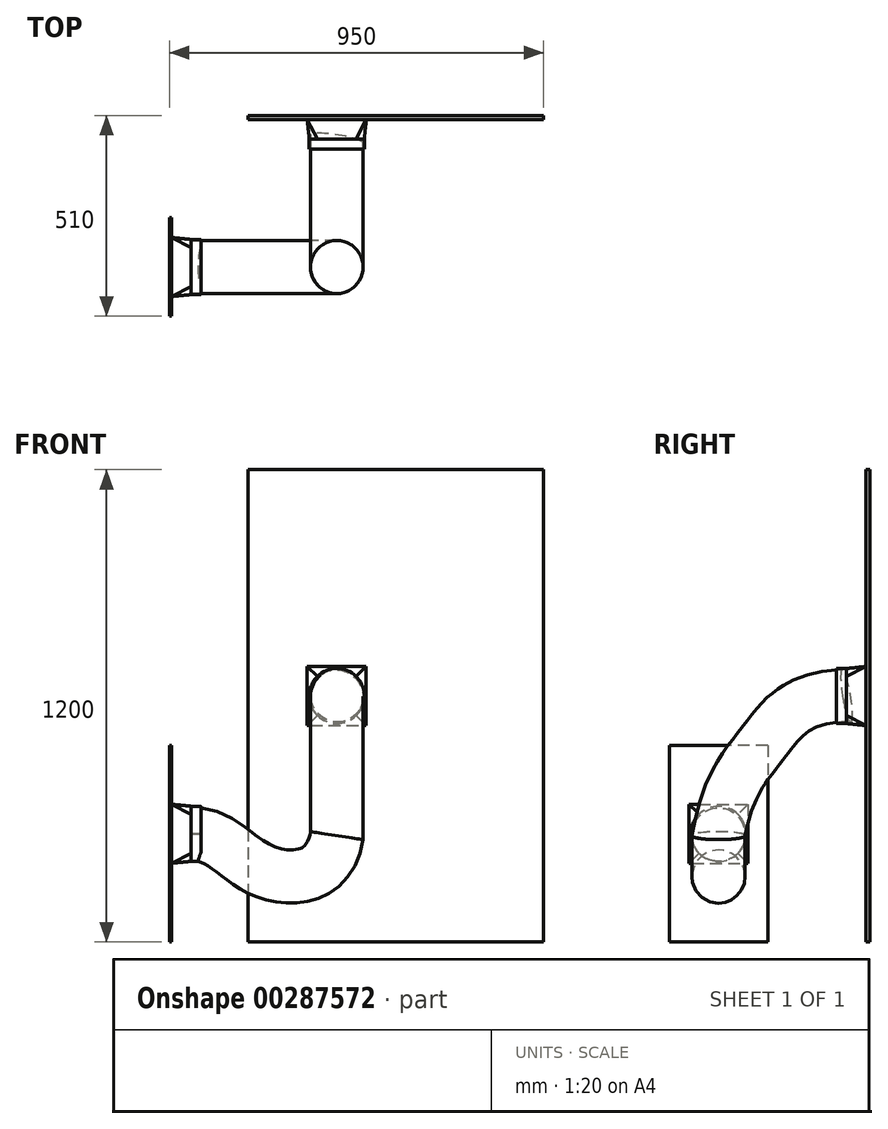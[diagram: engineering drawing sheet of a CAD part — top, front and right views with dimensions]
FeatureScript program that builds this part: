
annotation { "Feature Type Name" : "Feature", "Feature Type Description" : "" }
export const myFeature = defineFeature(function(context is Context, id is Id, definition is map)
    precondition{}
    {
        {
            var Q0;
            Q0=qCreatedBy(makeId("Top.planeOp"),FACE);
            var sketch = newSketch(context, id + "F0", { "sketchPlane" : qUnion([Q0])});
            skLineSegment(sketch, "E0.bottom", {"start": v(450, 450) * mm, "end": v(455, 450) * mm});
            skLineSegment(sketch, "E0.top", {"start": v(450, 200) * mm, "end": v(455, 200) * mm});
            skLineSegment(sketch, "E0.left", {"start": v(450, 450) * mm, "end": v(450, 200) * mm});
            skLineSegment(sketch, "E0.right", {"start": v(455, 450) * mm, "end": v(455, 200) * mm});
            skSolve(sketch);
        }
        {
            var Q0;
            Q0=makeQuery(id+"F0.imprint","IMPRINT",FACE,{"disambiguationData":[TD([[makeQuery(id+"F0.imprint","IMPRINT",EDGE,{"derivedFrom":sQuery(id+"F0.wireOp",EDGE,"E0.bottom")}),-1.0]])]});
            extrude(context, id + "F1", {"entities" : qUnion([Q0]), "depth" : 500 * mm});
        }
        {
            var Q0;
            Q0=qCreatedBy(makeId("Top.planeOp"),FACE);
            var sketch = newSketch(context, id + "F2", { "sketchPlane" : qUnion([Q0])});
            skLineSegment(sketch, "E1.bottom", {"start": v(650, 710) * mm, "end": v(1400, 710) * mm});
            skLineSegment(sketch, "E1.top", {"start": v(650, 700) * mm, "end": v(1400, 700) * mm});
            skLineSegment(sketch, "E1.left", {"start": v(650, 710) * mm, "end": v(650, 700) * mm});
            skLineSegment(sketch, "E1.right", {"start": v(1400, 710) * mm, "end": v(1400, 700) * mm});
            skSolve(sketch);
        }
        {
            var Q0;
            Q0=makeQuery(id+"F2.imprint","IMPRINT",FACE,{"disambiguationData":[TD([[makeQuery(id+"F2.imprint","IMPRINT",EDGE,{"derivedFrom":sQuery(id+"F2.wireOp",EDGE,"E1.bottom")}),-1.0]])]});
            extrude(context, id + "F3", {"entities" : qUnion([Q0]), "depth" : 1200 * mm});
        }
        {
            var Q0;
            Q0=makeQuery(id+"F1.opExtrude","SWEPT_FACE",FACE,{"disambiguationData":[OSD([sQuery(id+"F0.wireOp",EDGE,"E0.right")])]});
            var sketch = newSketch(context, id + "F4", { "sketchPlane" : qUnion([Q0])});
            skLineSegment(sketch, "E2.bottom", {"start": v(250, 350) * mm, "end": v(400, 350) * mm});
            skLineSegment(sketch, "E2.top", {"start": v(250, 200) * mm, "end": v(400, 200) * mm});
            skLineSegment(sketch, "E2.left", {"start": v(250, 350) * mm, "end": v(250, 200) * mm});
            skLineSegment(sketch, "E2.right", {"start": v(400, 350) * mm, "end": v(400, 200) * mm});
            skSolve(sketch);
        }
        {
            var Q0;
            Q0=makeQuery(id+"F4.imprint","IMPRINT",FACE,{"disambiguationData":[TD([[makeQuery(id+"F4.imprint","IMPRINT",EDGE,{"derivedFrom":sQuery(id+"F4.wireOp",EDGE,"E2.bottom")}),-1.0]])]});
            cPlane(context, id + "F5", {"entities" : qUnion([Q0]), "cplaneType" : CPlaneType.OFFSET, "offset" : 50 * mm, "width" : 150 * mm, "height" : 150 * mm});
        }
        {
            var Q0;
            Q0=qCreatedBy(id+"F5.planeOp",FACE);
            var sketch = newSketch(context, id + "F6", { "sketchPlane" : qUnion([Q0])});
            skCircle(sketch, "E3", {"center": v(325, 275) * mm, "radius": 70 * mm});
            skSolve(sketch);
        }
        {
            var Q1;
            Q1=makeQuery(id+"F4.imprint","IMPRINT",FACE,{"disambiguationData":[TD([[makeQuery(id+"F4.imprint","IMPRINT",EDGE,{"derivedFrom":sQuery(id+"F4.wireOp",EDGE,"E2.bottom")}),-1.0]])]});
            var Q2;
            Q2=makeQuery(id+"F6.imprint","IMPRINT",FACE,{"disambiguationData":[TD([[makeQuery(id+"F6.imprint","IMPRINT",EDGE,{"derivedFrom":sQuery(id+"F6.wireOp",EDGE,"E3")}),1.0]])]});
            loft(context, id + "F7", {"operationType" : NewBodyOperationType.ADD, "sheetProfilesArray" : [{ "sheetProfileEntities" : qUnion([Q1]) }, { "sheetProfileEntities" : qUnion([Q2]) }]});
        }
        {
            var Q0;
            Q0=makeQuery(id+"F3.opExtrude","SWEPT_FACE",FACE,{"disambiguationData":[OSD([sQuery(id+"F2.wireOp",EDGE,"E1.top")])]});
            var sketch = newSketch(context, id + "F8", { "sketchPlane" : qUnion([Q0])});
            skLineSegment(sketch, "E4.bottom", {"start": v(800, 700) * mm, "end": v(950, 700) * mm});
            skLineSegment(sketch, "E4.top", {"start": v(800, 550) * mm, "end": v(950, 550) * mm});
            skLineSegment(sketch, "E4.left", {"start": v(800, 700) * mm, "end": v(800, 550) * mm});
            skLineSegment(sketch, "E4.right", {"start": v(950, 700) * mm, "end": v(950, 550) * mm});
            skSolve(sketch);
        }
        {
            var Q0;
            Q0=makeQuery(id+"F8.imprint","IMPRINT",FACE,{"disambiguationData":[TD([[makeQuery(id+"F8.imprint","IMPRINT",EDGE,{"derivedFrom":sQuery(id+"F8.wireOp",EDGE,"E4.bottom")}),-1.0]])]});
            cPlane(context, id + "F9", {"entities" : qUnion([Q0]), "cplaneType" : CPlaneType.OFFSET, "offset" : 50 * mm, "width" : 150 * mm, "height" : 150 * mm});
        }
        {
            var Q0;
            Q0=qCreatedBy(id+"F9.planeOp",FACE);
            var sketch = newSketch(context, id + "F10", { "sketchPlane" : qUnion([Q0])});
            skCircle(sketch, "E5", {"center": v(875, 625) * mm, "radius": 70 * mm});
            skSolve(sketch);
        }
        {
            var Q1;
            Q1=makeQuery(id+"F8.imprint","IMPRINT",FACE,{"disambiguationData":[TD([[makeQuery(id+"F8.imprint","IMPRINT",EDGE,{"derivedFrom":sQuery(id+"F8.wireOp",EDGE,"E4.bottom")}),-1.0]])]});
            var Q2;
            Q2=makeQuery(id+"F10.imprint","IMPRINT",FACE,{"disambiguationData":[TD([[makeQuery(id+"F10.imprint","IMPRINT",EDGE,{"derivedFrom":sQuery(id+"F10.wireOp",EDGE,"E5")}),1.0]])]});
            loft(context, id + "F11", {"operationType" : NewBodyOperationType.ADD, "sheetProfilesArray" : [{ "sheetProfileEntities" : qUnion([Q1]) }, { "sheetProfileEntities" : qUnion([Q2]) }]});
        }
        {
            var Q0;
            Q0=makeQuery(id+"F1.opExtrude","SWEPT_FACE",FACE,{"disambiguationData":[OSD([sQuery(id+"F0.wireOp",EDGE,"E0.top")])]});
            cPlane(context, id + "F12", {"entities" : qUnion([Q0]), "cplaneType" : CPlaneType.OFFSET, "offset" : 125 * mm, "oppositeDirection" : true, "width" : 150 * mm, "height" : 150 * mm});
        }
        {
            var Q0;
            Q0=qCreatedBy(id+"F12.planeOp",FACE);
            var sketch = newSketch(context, id + "F13", { "sketchPlane" : qUnion([Q0])});
            skFitSpline(sketch, "E6", {"points": [v(505, 275) * mm, v(686.19, 181.56) * mm, v(875, 270.24) * mm], "startDerivative": vector(486.4, -7.04) * mm, "endDerivative": vector(101.55, 675.06) * mm});
            skSolve(sketch);
        }
        {
            var Q0;
            Q0=sQuery(id+"F13.wireOp",EDGE,"E6");
            var Q1;
            Q1=sQuery(id+"F13.wireOp",VERTEX,"E6.2.internal");
            cPlane(context, id + "F14", {"entities" : qUnion([Q0, Q1]), "cplaneType" : CPlaneType.CURVE_POINT, "offset" : 25 * mm, "width" : 150 * mm, "height" : 150 * mm});
        }
        {
            var Q0;
            Q0=makeQuery(id+"F3.opExtrude","SWEPT_FACE",FACE,{"disambiguationData":[OSD([sQuery(id+"F2.wireOp",EDGE,"E1.left")])]});
            cPlane(context, id + "F15", {"entities" : qUnion([Q0]), "cplaneType" : CPlaneType.OFFSET, "offset" : 225 * mm, "oppositeDirection" : true, "width" : 150 * mm, "height" : 150 * mm});
        }
        {
            var Q0;
            Q0=qCreatedBy(id+"F15.planeOp",FACE);
            var sketch = newSketch(context, id + "F16", { "sketchPlane" : qUnion([Q0])});
            skFitSpline(sketch, "E7", {"points": [v(-650, 625) * mm, v(-436.96, 504.63) * mm, v(-325, 270.24) * mm], "startDerivative": vector(785.67, 5.26) * mm, "endDerivative": vector(133.48, -764.38) * mm});
            skSolve(sketch);
        }
        {
            var Q0;
            Q0=qCreatedBy(id+"F14.planeOp",FACE);
            var sketch = newSketch(context, id + "F17", { "sketchPlane" : qUnion([Q0])});
            skCircle(sketch, "E8", {"center": v(825.07, 325) * mm, "radius": 67.5 * mm});
            skSolve(sketch);
        }
        {
            var Q0;
            Q0=makeQuery(id+"F17.imprint","IMPRINT",FACE,{"disambiguationData":[TD([[makeQuery(id+"F17.imprint","IMPRINT",EDGE,{"derivedFrom":sQuery(id+"F17.wireOp",EDGE,"E8")}),1.0]])]});
            var Q1;
            Q1=sQuery(id+"F13.wireOp",EDGE,"E6");
            sweep(context, id + "F18", {"operationType" : NewBodyOperationType.ADD, "profiles" : qUnion([Q0]), "path" : qUnion([Q1])});
        }
        {
            var Q0;
            Q0=makeQuery(id+"F18.opSweep","CAP_FACE",FACE,{"disambiguationData":[OSD([sQuery(id+"F13.wireOp",VERTEX,"E6.end"),sQuery(id+"F17.wireOp",EDGE,"E8")])],"isStart":true});
            var Q1;
            Q1=sQuery(id+"F16.wireOp",EDGE,"E7");
            sweep(context, id + "F19", {"profiles" : qUnion([Q0]), "path" : qUnion([Q1])});
        }
        {
            var Q0;
            Q0=makeQuery(id+"F11.opLoft","CAP_FACE",FACE,{"disambiguationData":[OSD([makeQuery(id+"F10.imprint","IMPRINT",FACE,{"disambiguationData":[TD([[makeQuery(id+"F10.imprint","IMPRINT",EDGE,{"derivedFrom":sQuery(id+"F10.wireOp",EDGE,"E5")}),1.0]])]})])],"isStart":true});
            extrude(context, id + "F20", {"entities" : qUnion([Q0]), "depth" : 25 * mm});
        }
        {
            var Q0;
            Q0=makeQuery(id+"F7.opLoft","CAP_FACE",FACE,{"disambiguationData":[OSD([makeQuery(id+"F6.imprint","IMPRINT",FACE,{"disambiguationData":[TD([[makeQuery(id+"F6.imprint","IMPRINT",EDGE,{"derivedFrom":sQuery(id+"F6.wireOp",EDGE,"E3")}),1.0]])]})])],"isStart":true});
            extrude(context, id + "F21", {"entities" : qUnion([Q0]), "operationType" : NewBodyOperationType.ADD, "depth" : 25 * mm});
        }
    });
